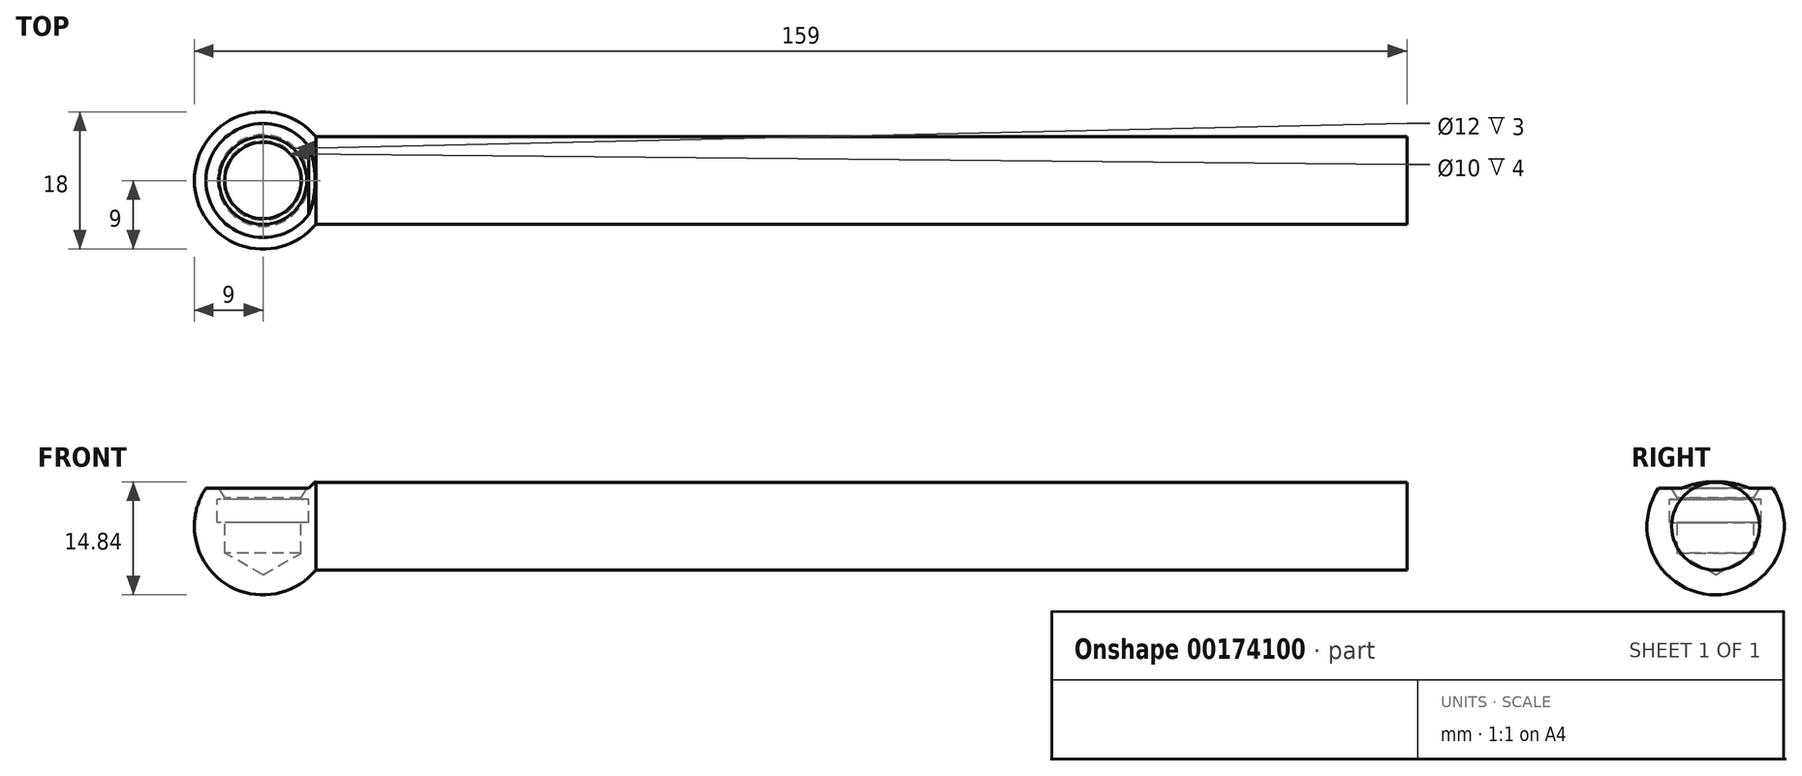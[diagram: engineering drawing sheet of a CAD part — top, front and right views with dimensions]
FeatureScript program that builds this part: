
annotation { "Feature Type Name" : "Feature", "Feature Type Description" : "" }
export const myFeature = defineFeature(function(context is Context, id is Id, definition is map)
    precondition{}
    {
        {
            var Q0;
            Q0=qCreatedBy(makeId("Front.planeOp"),FACE);
            var sketch = newSketch(context, id + "F0", { "sketchPlane" : qUnion([Q0])});
            skLineSegment(sketch, "E0", {"start": v(0, 0) * mm, "end": v(241.1, 0) * mm, "construction": true});
            skArc(sketch, "E1", {"start": v(6.92, 5.75) * mm, "mid": v(-3.06, 8.47) * mm, "end": v(-9, 0) * mm});
            skLineSegment(sketch, "E2", {"start": v(6.92, 5.75) * mm, "end": v(150, 5.75) * mm});
            skLineSegment(sketch, "E3", {"start": v(150, 5.75) * mm, "end": v(150, 0) * mm});
            skLineSegment(sketch, "E4", {"start": v(150, 0) * mm, "end": v(-9, 0) * mm});
            skSolve(sketch);
        }
        {
            var Q0;
            Q0=makeQuery(id+"F0.imprint","IMPRINT",FACE,{"disambiguationData":[TD([[makeQuery(id+"F0.imprint","IMPRINT",EDGE,{"derivedFrom":sQuery(id+"F0.wireOp",EDGE,"E1")}),1.0]])]});
            var Q1;
            Q1=sQuery(id+"F0.wireOp",EDGE,"E0");
            revolve(context, id + "F1", {"entities" : qUnion([Q0]), "axis" : qUnion([Q1]), "revolveType" : RevolveType.FULL});
        }
        {
            var Q0;
            Q0=qCreatedBy(makeId("Front.planeOp"),FACE);
            var sketch = newSketch(context, id + "F2", { "sketchPlane" : qUnion([Q0])});
            skLineSegment(sketch, "E5", {"start": v(10, 10) * mm, "end": v(-10, 10) * mm});
            skLineSegment(sketch, "E6", {"start": v(-10, 10) * mm, "end": v(-10, 5) * mm});
            skLineSegment(sketch, "E7", {"start": v(-10, 5) * mm, "end": v(6, 5) * mm});
            skLineSegment(sketch, "E8", {"start": v(6, 5) * mm, "end": v(10, 9) * mm});
            skLineSegment(sketch, "E9", {"start": v(10, 9) * mm, "end": v(10, 10) * mm});
            skSolve(sketch);
        }
        {
            var Q0;
            Q0=makeQuery(id+"F2.imprint","IMPRINT",FACE,{"disambiguationData":[TD([[makeQuery(id+"F2.imprint","IMPRINT",EDGE,{"derivedFrom":sQuery(id+"F2.wireOp",EDGE,"E5")}),1.0]])]});
            extrude(context, id + "F3", {"entities" : qUnion([Q0]), "operationType" : NewBodyOperationType.REMOVE, "oppositeDirection" : true, "depth" : 25 * mm, "hasSecondDirection" : true, "secondDirectionOppositeDirection" : false, "secondDirectionDepth" : 25 * mm});
        }
        {
            var Q0;
            Q0=qCreatedBy(makeId("Front.planeOp"),FACE);
            var sketch = newSketch(context, id + "F4", { "sketchPlane" : qUnion([Q0])});
            skLineSegment(sketch, "E10", {"start": v(0, -6.39) * mm, "end": v(0, 5) * mm});
            skLineSegment(sketch, "E11", {"start": v(0, 5) * mm, "end": v(-5.75, 5) * mm});
            skLineSegment(sketch, "E12", {"start": v(-5.75, 5) * mm, "end": v(-5, 3.7) * mm});
            skLineSegment(sketch, "E13", {"start": v(-5.2, 3.5) * mm, "end": v(-6, 3.5) * mm});
            skLineSegment(sketch, "E14", {"start": v(-6, 3.5) * mm, "end": v(-6, 0.5) * mm});
            skLineSegment(sketch, "E15", {"start": v(-6, 0.5) * mm, "end": v(-5, 0.5) * mm});
            skLineSegment(sketch, "E16", {"start": v(-5, 0.5) * mm, "end": v(-5, -3.5) * mm});
            skLineSegment(sketch, "E17", {"start": v(-5, -3.5) * mm, "end": v(0, -6.39) * mm});
            skLineSegment(sketch, "E18", {"start": v(-5.2, 3.5) * mm, "end": v(-5, 3.7) * mm});
            skLineSegment(sketch, "E19", {"start": v(0, 0) * mm, "end": v(0, 12.84) * mm, "construction": true});
            skSolve(sketch);
        }
        {
            var Q0;
            Q0 = qSketchRegion(id + "F4", true);
            var Q1;
            Q1=sQuery(id+"F4.wireOp",EDGE,"E19");
            revolve(context, id + "F5", {"operationType" : NewBodyOperationType.REMOVE, "entities" : qUnion([Q0]), "axis" : qUnion([Q1]), "revolveType" : RevolveType.FULL, "oppositeDirection" : true});
        }
    });
